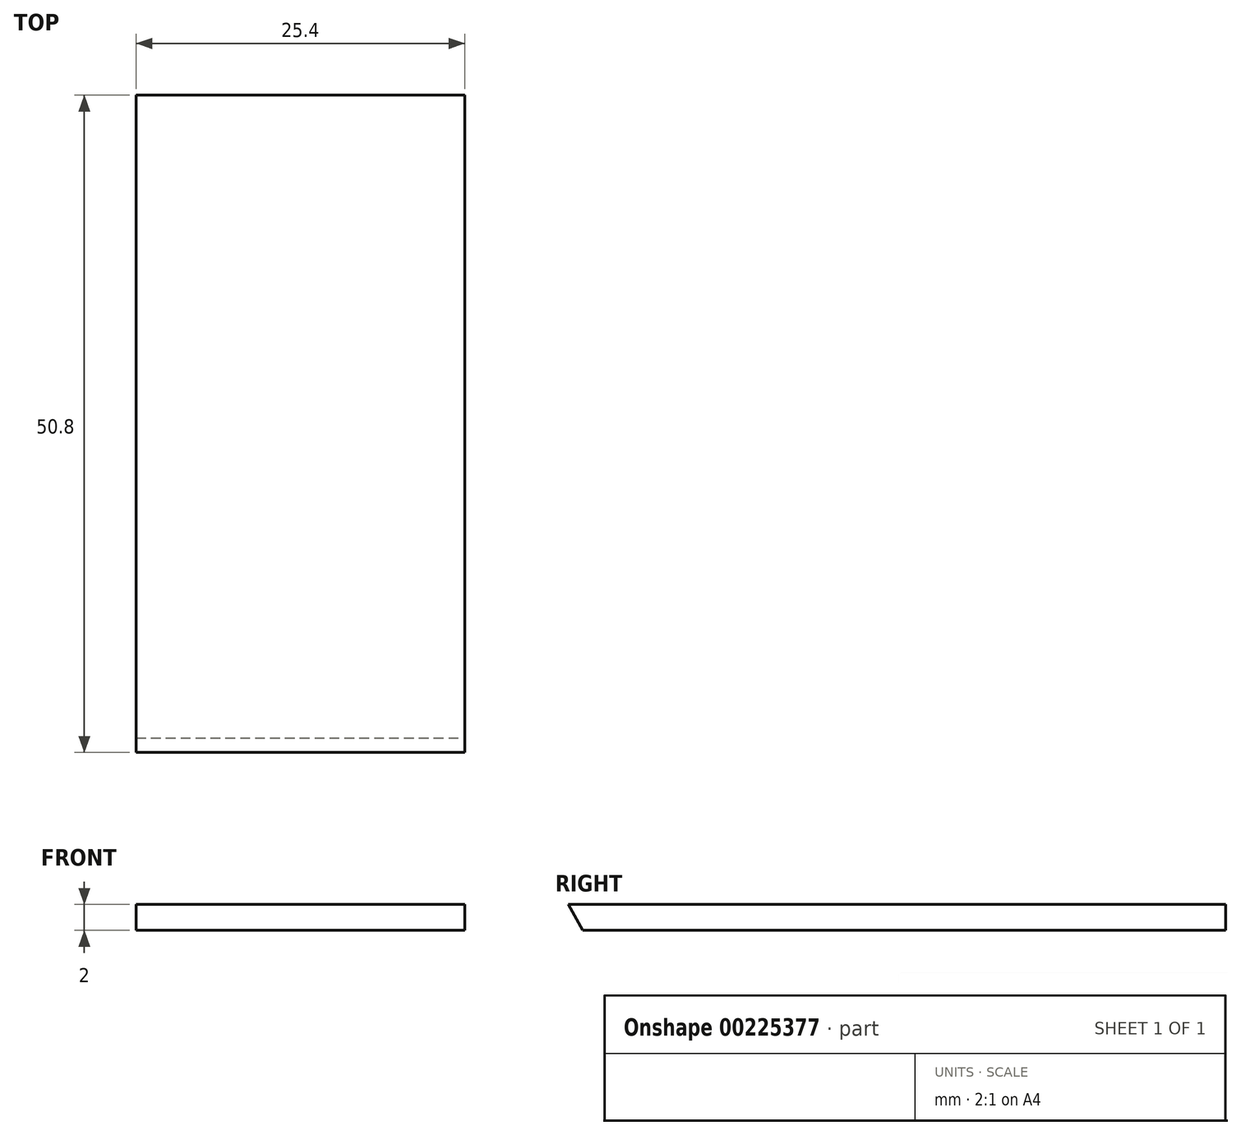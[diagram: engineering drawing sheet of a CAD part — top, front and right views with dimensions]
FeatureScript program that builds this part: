
annotation { "Feature Type Name" : "Feature", "Feature Type Description" : "" }
export const myFeature = defineFeature(function(context is Context, id is Id, definition is map)
    precondition{}
    {
        {
            var Q0;
            Q0=qCreatedBy(makeId("Top.planeOp"),FACE);
            var sketch = newSketch(context, id + "F0", { "sketchPlane" : qUnion([Q0])});
            skLineSegment(sketch, "E0.bottom", {"start": v(12.7, -25.4) * mm, "end": v(-12.7, -25.4) * mm});
            skLineSegment(sketch, "E0.top", {"start": v(12.7, 25.4) * mm, "end": v(-12.7, 25.4) * mm});
            skLineSegment(sketch, "E0.left", {"start": v(12.7, -25.4) * mm, "end": v(12.7, 25.4) * mm});
            skLineSegment(sketch, "E0.right", {"start": v(-12.7, -25.4) * mm, "end": v(-12.7, 25.4) * mm});
            skPoint(sketch, "E0.middle", {"position": v(0, 0) * mm});
            skSolve(sketch);
        }
        {
            var Q0;
            Q0=makeQuery(id+"F0.imprint","IMPRINT",FACE,{"disambiguationData":[TD([[makeQuery(id+"F0.imprint","IMPRINT",EDGE,{"derivedFrom":sQuery(id+"F0.wireOp",EDGE,"E0.bottom")}),-1.0]])]});
            extrude(context, id + "F1", {"entities" : qUnion([Q0]), "depth" : 2 * mm});
        }
        {
            var Q0;
            Q0=makeQuery(id+"F1.opExtrude","SWEPT_FACE",FACE,{"disambiguationData":[OSD([sQuery(id+"F0.wireOp",EDGE,"E0.left")])]});
            var sketch = newSketch(context, id + "F2", { "sketchPlane" : qUnion([Q0])});
            skLineSegment(sketch, "E1", {"start": v(-25.4, 2) * mm, "end": v(-24.3, 0) * mm});
            skLineSegment(sketch, "E2", {"start": v(-24.3, 0) * mm, "end": v(-25.4, 0) * mm});
            skLineSegment(sketch, "E3", {"start": v(-25.4, 0) * mm, "end": v(-25.4, 2) * mm});
            skSolve(sketch);
        }
        {
            var Q0;
            Q0=makeQuery(id+"F2.imprint","IMPRINT",FACE,{"disambiguationData":[TD([[makeQuery(id+"F2.imprint","IMPRINT",EDGE,{"derivedFrom":sQuery(id+"F2.wireOp",EDGE,"E1")}),-1.0]])]});
            extrude(context, id + "F3", {"entities" : qUnion([Q0]), "operationType" : NewBodyOperationType.REMOVE, "oppositeDirection" : true, "depth" : 25.4 * mm});
        }
    });
